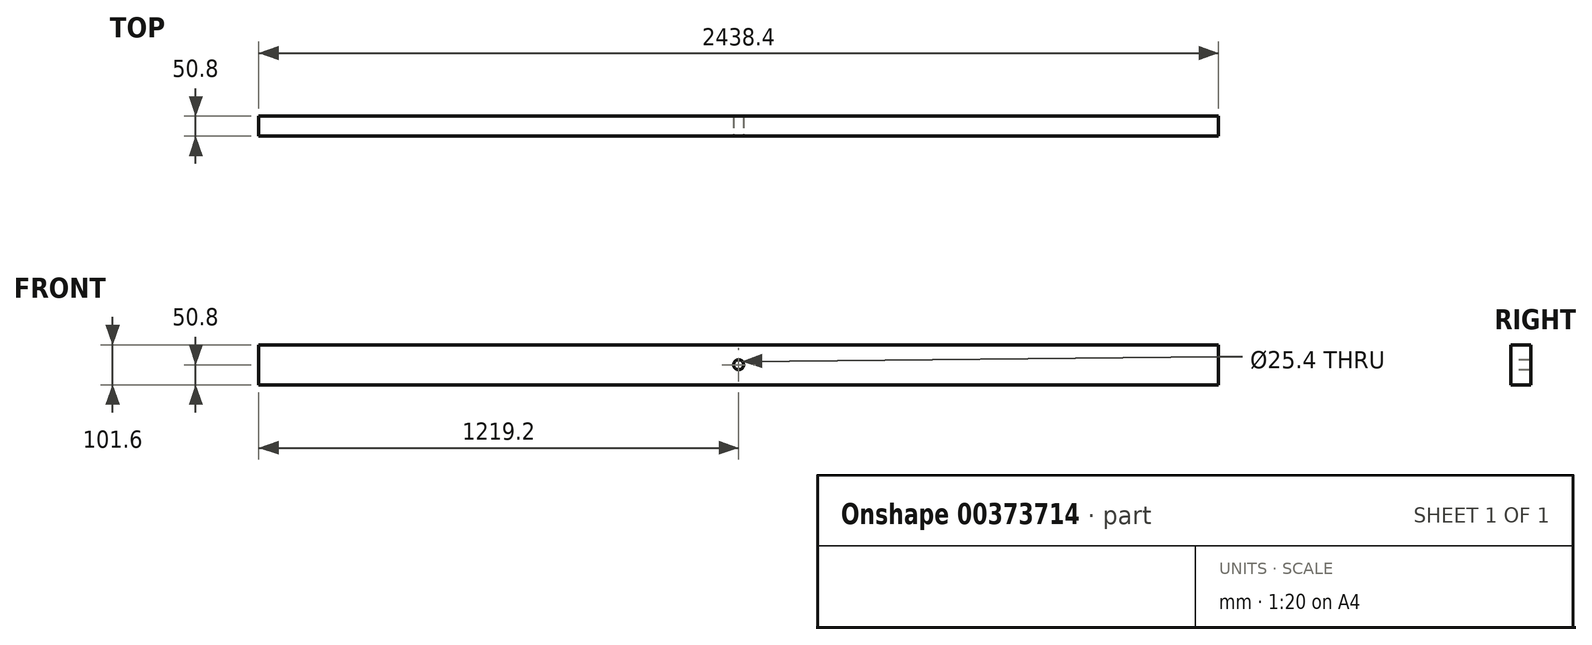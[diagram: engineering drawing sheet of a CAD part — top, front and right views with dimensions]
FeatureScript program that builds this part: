
annotation { "Feature Type Name" : "Feature", "Feature Type Description" : "" }
export const myFeature = defineFeature(function(context is Context, id is Id, definition is map)
    precondition{}
    {
        {
            var Q0;
            Q0=qCreatedBy(makeId("Right.planeOp"),FACE);
            var sketch = newSketch(context, id + "F0", { "sketchPlane" : qUnion([Q0])});
            skLineSegment(sketch, "E0.bottom", {"start": v(-25.4, 50.8) * mm, "end": v(25.4, 50.8) * mm});
            skLineSegment(sketch, "E0.top", {"start": v(-25.4, -50.8) * mm, "end": v(25.4, -50.8) * mm});
            skLineSegment(sketch, "E0.left", {"start": v(-25.4, 50.8) * mm, "end": v(-25.4, -50.8) * mm});
            skLineSegment(sketch, "E0.right", {"start": v(25.4, 50.8) * mm, "end": v(25.4, -50.8) * mm});
            skLineSegment(sketch, "E1", {"start": v(-25.4, 0) * mm, "end": v(25.4, 0) * mm, "construction": true});
            skLineSegment(sketch, "E2", {"start": v(0, 50.8) * mm, "end": v(0, -50.8) * mm, "construction": true});
            skSolve(sketch);
        }
        {
            var Q0;
            Q0 = qSketchRegion(id + "F0", true);
            extrude(context, id + "F1", {"entities" : qUnion([Q0]), "endBound" : BoundingType.SYMMETRIC, "depth" : 2438.4 * mm});
        }
        {
            var Q0;
            Q0=qCreatedBy(makeId("Front.planeOp"),FACE);
            var sketch = newSketch(context, id + "F2", { "sketchPlane" : qUnion([Q0])});
            skCircle(sketch, "E3", {"center": v(0, 0) * mm, "radius": 12.7 * mm});
            skSolve(sketch);
        }
        {
            var Q0;
            Q0 = qSketchRegion(id + "F2", true);
            extrude(context, id + "F3", {"entities" : qUnion([Q0]), "operationType" : NewBodyOperationType.REMOVE, "endBound" : BoundingType.THROUGH_ALL, "oppositeDirection" : true, "depth" : 25.4 * mm, "hasSecondDirection" : true, "secondDirectionBound" : SecondDirectionBoundingType.THROUGH_ALL, "secondDirectionOppositeDirection" : false, "secondDirectionDepth" : 25.4 * mm});
        }
    });
